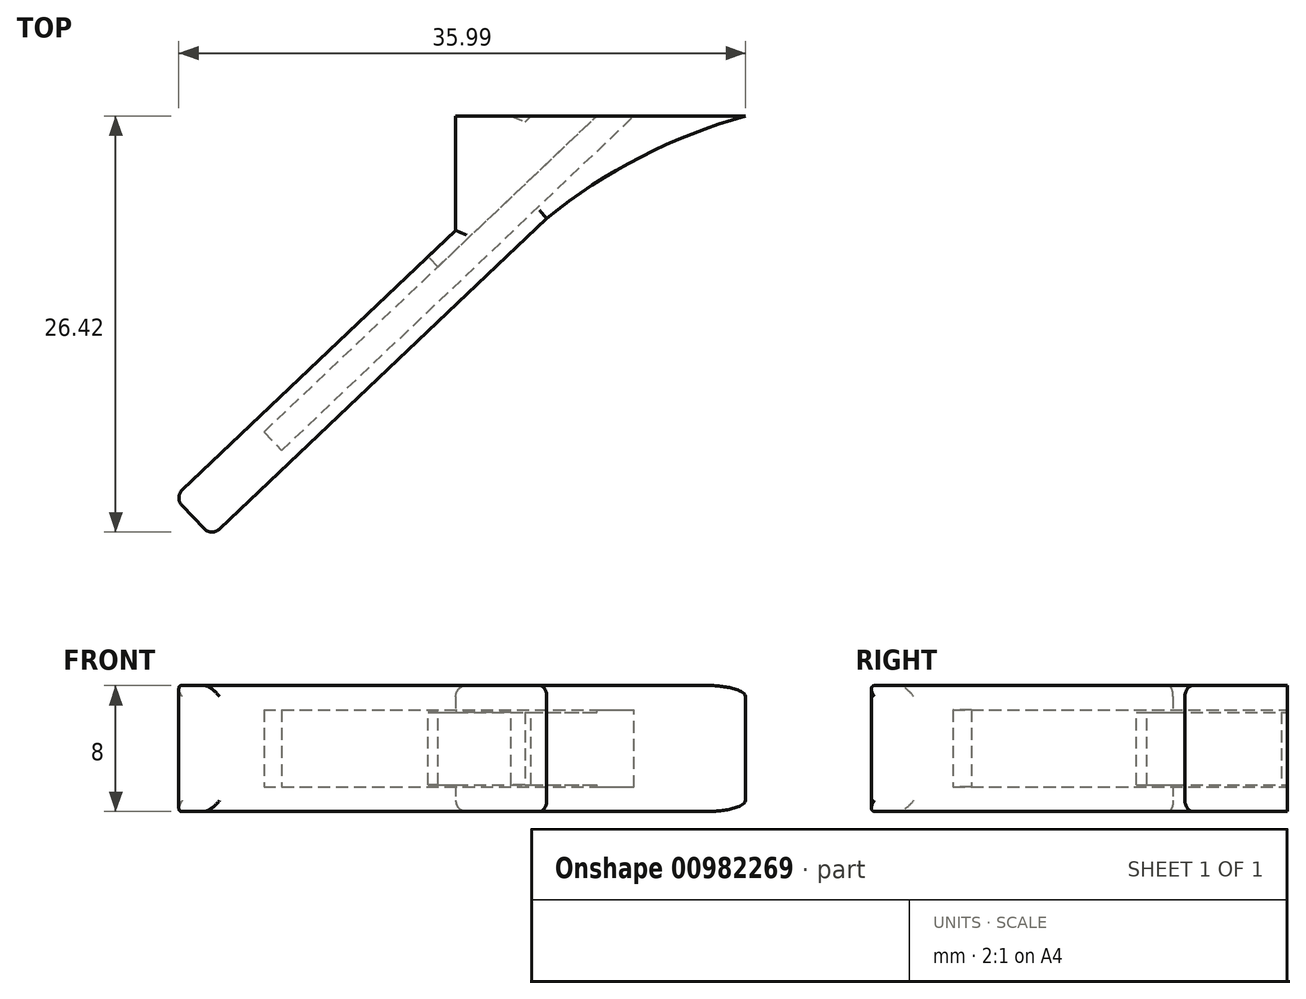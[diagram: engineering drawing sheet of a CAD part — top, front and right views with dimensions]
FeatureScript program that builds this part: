
annotation { "Feature Type Name" : "Feature", "Feature Type Description" : "" }
export const myFeature = defineFeature(function(context is Context, id is Id, definition is map)
    precondition{}
    {
        {
            var Q0;
            Q0=qCreatedBy(makeId("Top.planeOp"),FACE);
            var sketch = newSketch(context, id + "F0", { "sketchPlane" : qUnion([Q0])});
            skLineSegment(sketch, "E0", {"start": v(-32.51, 0) * mm, "end": v(2.5, 0) * mm, "construction": true});
            skLineSegment(sketch, "E1", {"start": v(-19.27, -20.65) * mm, "end": v(2.5, 0) * mm, "construction": true});
            skLineSegment(sketch, "E2", {"start": v(-67.16, -38.53) * mm, "end": v(-47.16, -38.1) * mm});
            skLineSegment(sketch, "E3", {"start": v(-19.83, -20.06) * mm, "end": v(1.3, 0) * mm});
            skLineSegment(sketch, "E4", {"start": v(-18.7, -21.24) * mm, "end": v(3.68, 0) * mm});
            skLineSegment(sketch, "E5", {"start": v(-19.83, -20.06) * mm, "end": v(-18.7, -21.24) * mm});
            skPoint(sketch, "E6.positionSnap0", {"position": v(-19.27, -20.65) * mm});
            skLineSegment(sketch, "E7", {"start": v(15.29, 0) * mm, "end": v(15.29, -6.53) * mm, "construction": true});
            skPoint(sketch, "E8", {"position": v(2.5, 0) * mm});
            skLineSegment(sketch, "E9", {"start": v(2.5, 0) * mm, "end": v(15.29, 0) * mm});
            skLineSegment(sketch, "E10.0", {"start": v(-25.53, -24.23) * mm, "end": v(0, 0) * mm});
            skLineSegment(sketch, "E11.0", {"start": v(-23.17, -26.71) * mm, "end": v(4.98, 0) * mm});
            skLineSegment(sketch, "E12.0", {"start": v(-25.53, -24.23) * mm, "end": v(-23.17, -26.71) * mm});
            skSolve(sketch);
        }
        {
            var Q0;
            Q0=qCreatedBy(makeId("Top.planeOp"),FACE);
            var sketch = newSketch(context, id + "F1", { "sketchPlane" : qUnion([Q0])});
            skLineSegment(sketch, "E13.0", {"start": v(-25.53, -24.23) * mm, "end": v(0, 0) * mm});
            skLineSegment(sketch, "E14.0", {"start": v(-25.53, -24.23) * mm, "end": v(-23.17, -26.71) * mm});
            skLineSegment(sketch, "E15.0", {"start": v(-23.17, -26.71) * mm, "end": v(4.98, 0) * mm});
            skLineSegment(sketch, "E16", {"start": v(0, 0) * mm, "end": v(4.98, 0) * mm});
            skLineSegment(sketch, "E17", {"start": v(-7.65, -7.26) * mm, "end": v(-7.65, 0) * mm});
            skLineSegment(sketch, "E18", {"start": v(-7.65, 0) * mm, "end": v(0, 0) * mm});
            skLineSegment(sketch, "E19", {"start": v(4.98, 0) * mm, "end": v(10.75, 0) * mm});
            skArc(sketch, "E20", {"start": v(10.75, 0) * mm, "mid": v(1.74, -3.94) * mm, "end": v(-5.8, -10.24) * mm});
            skPoint(sketch, "E20.second.point", {"position": v(-1.87, -6.5) * mm});
            skPoint(sketch, "E20.third.point", {"position": v(4.01, -2.65) * mm});
            skSolve(sketch);
        }
        {
            var Q0;
            Q0 = qSketchRegion(id + "F1", true);
            extrude(context, id + "F2", {"entities" : qUnion([Q0]), "endBound" : BoundingType.SYMMETRIC, "depth" : 8 * mm, "offsetDistance" : 25 * mm});
        }
        {
            var Q0;
            Q0=qCreatedBy(makeId("Top.planeOp"),FACE);
            var sketch = newSketch(context, id + "F3", { "sketchPlane" : qUnion([Q0])});
            skLineSegment(sketch, "E21.0", {"start": v(-18.7, -21.24) * mm, "end": v(6.31, 2.5) * mm});
            skLineSegment(sketch, "E22.0", {"start": v(-19.83, -20.06) * mm, "end": v(-18.7, -21.24) * mm});
            skLineSegment(sketch, "E23.0", {"start": v(-19.83, -20.06) * mm, "end": v(3.94, 2.5) * mm});
            skLineSegment(sketch, "E24", {"start": v(3.94, 2.5) * mm, "end": v(6.31, 2.5) * mm});
            skPoint(sketch, "E25.orphan", {"position": v(1.3, 0) * mm});
            skPoint(sketch, "E26.orphan", {"position": v(3.68, 0) * mm});
            skSolve(sketch);
        }
        {
            var Q0;
            Q0 = qSketchRegion(id + "F3", true);
            extrude(context, id + "F4", {"entities" : qUnion([Q0]), "operationType" : NewBodyOperationType.REMOVE, "endBound" : BoundingType.SYMMETRIC, "depth" : 4.9 * mm, "offsetDistance" : 25 * mm});
        }
        {
            var Q0;
            Q0=qCreatedBy(makeId("Top.planeOp"),FACE);
            var sketch = newSketch(context, id + "F5", { "sketchPlane" : qUnion([Q0])});
            skLineSegment(sketch, "E27.0", {"start": v(-19.83, -20.06) * mm, "end": v(1.3, 0) * mm});
            skLineSegment(sketch, "E28", {"start": v(-8.26, -10.13) * mm, "end": v(-10.76, -7.49) * mm});
            skLineSegment(sketch, "E29", {"start": v(-10.76, -7.49) * mm, "end": v(-0.3, 2.44) * mm});
            skLineSegment(sketch, "E30", {"start": v(-0.3, 2.44) * mm, "end": v(2.2, -0.2) * mm});
            skLineSegment(sketch, "E31", {"start": v(-8.26, -10.13) * mm, "end": v(2.2, -0.2) * mm});
            skSolve(sketch);
        }
        {
            var Q0;
            Q0 = qSketchRegion(id + "F5", true);
            extrude(context, id + "F6", {"entities" : qUnion([Q0]), "operationType" : NewBodyOperationType.REMOVE, "endBound" : BoundingType.SYMMETRIC, "depth" : 4.6 * mm, "offsetDistance" : 25 * mm});
        }
        {
            var Q0;
            Q0=makeQuery(id+"F6.boolean.opBoolean","INTERSECT",EDGE,{"derivedFrom":[makeQuery(id+"F2.opExtrude","SWEPT_FACE",FACE,{"disambiguationData":[OSD([sQuery(id+"F1.wireOp",EDGE,"E17")])]}),makeQuery(id+"F6.opExtrude","SWEPT_FACE",FACE,{"disambiguationData":[OSD([sQuery(id+"F5.wireOp",EDGE,"E29")])]})]});
            chamfer(context, id + "F7", {"entities" : qUnion([Q0]), "width" : 2.6 * mm, "tangentPropagation" : true});
        }
        {
            var Q0;
            Q0=makeQuery(id+"F2.opExtrude","CAP_EDGE",EDGE,{"disambiguationData":[OSD([sQuery(id+"F1.wireOp",EDGE,"E15.0")])],"isStart":false});
            var Q1;
            Q1=makeQuery(id+"F2.opExtrude","CAP_EDGE",EDGE,{"disambiguationData":[OSD([sQuery(id+"F1.wireOp",EDGE,"E15.0")])],"isStart":true});
            var Q2;
            Q2=makeQuery(id+"F2.opExtrude","CAP_EDGE",EDGE,{"disambiguationData":[OSD([sQuery(id+"F1.wireOp",EDGE,"E13.0")])],"isStart":false});
            var Q3;
            Q3=makeQuery(id+"F2.opExtrude","CAP_EDGE",EDGE,{"disambiguationData":[OSD([sQuery(id+"F1.wireOp",EDGE,"E13.0")])],"isStart":true});
            var Q4;
            Q4=makeQuery(id+"F2.opExtrude","CAP_EDGE",EDGE,{"disambiguationData":[OSD([sQuery(id+"F1.wireOp",EDGE,"E17")])],"isStart":false});
            var Q5;
            Q5=makeQuery(id+"F2.opExtrude","CAP_EDGE",EDGE,{"disambiguationData":[OSD([sQuery(id+"F1.wireOp",EDGE,"E17")])],"isStart":true});
            var Q6;
            Q6=makeQuery(id+"F2.opExtrude","SWEPT_EDGE",EDGE,{"disambiguationData":[OSD([sQuery(id+"F1.wireOp",EDGE,"E13.0"),sQuery(id+"F1.wireOp",EDGE,"E14.0")])]});
            var Q7;
            Q7=makeQuery(id+"F2.opExtrude","SWEPT_EDGE",EDGE,{"disambiguationData":[OSD([sQuery(id+"F1.wireOp",EDGE,"E14.0"),sQuery(id+"F1.wireOp",EDGE,"E15.0")])]});
            fillet(context, id + "F8", {"entities" : qUnion([Q0, Q1, Q2, Q3, Q4, Q5, Q6, Q7]), "tangentPropagation" : true, "radius" : 0.7 * mm, "defaultsChanged" : false, "vertexSettings" : [], "allowEdgeOverflow" : false});
        }
    });
